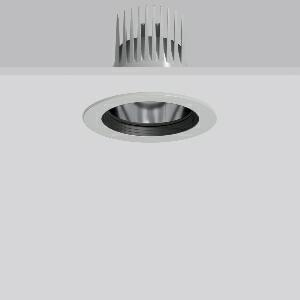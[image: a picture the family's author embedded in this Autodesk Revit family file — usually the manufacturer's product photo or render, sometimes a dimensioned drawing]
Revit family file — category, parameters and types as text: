
# Revit family: heledon_maxi_e_901759_004_94ef
name_source: partatom
category: Lighting Fixtures
units: mm (PartAtom-declared; Revit-internal decimal feet)

## family parameters
Cut with Voids When Loaded = No
Host = Face
Light Source = No
Part Type = Normal
Room Calculation Point = No
Round Connector Dimension = Use Diameter
Shared = No

## types (1)
- HELEDON maxi E (1 x LED Modul 930, 3250 lm, 3000)
    Apparent Load = 25 VA
    Approval mark = CE
    CIE Flux Codes = 97 100 100 100 100
    Color Rendering = 90
    Color Temperature = 3000
    Default Elevation = 1800 mm
    Description = Series: HELEDON maxi
Round recessed downlight. Housing: die-cast aluminium, powder-coated. Black plastic ring and recessed LED to prevent glare from the side. Optical assembly with reflector made of MIRO-Silver with 98% total light reflection for outstanding efficiency - can be changed without tools. Best colour rendering index Ra>90. Suitable for Recessed ceiling mounting. Installation without tools thanks to spring fastening system. Including separate LED converter with connecting cable 600 mm.High quality converter without flickering and stroboscopic effect. Through-wiring box (5 pole) available as accessory. The following accessories can be mounted without use of tools: interchangeable lenses, decorative glasses, honeycomb louvre, clear and frosted diffusers, white interchangeable plastic ring. 
Colour: silver
Diameter: 162 mm
Height: 3 mm
Cut-out diameter: 152 mm
Recess height: 200 mm
Luminaire: recess height: 135 mm
Lamp: LED
Socket: without socket
Colour temperature: 3000K
Colour rendering index (CRI): 92
System power: 25 W
Rated luminous flux: 3250 lm
Luminous efficiency: 130 lm/W
Control gear: Regulated power supply
Protection class: II
Type of protection: IP 20
    Height = 0 mm  [stored 0 ft]
    Lamp = 1 x LED Modul 930
    Lamp Light Flux = 3250 lm
    Lamp count = 1
    Length = 162 mm
    Lifetime = 50000 h
    Luminous efficacy = 130 lm/W
    Manufacturer = RZB
    ModVariant = No
    Model = 901759.004
    Mounting Place = Ceiling
    Mounting Type = Recessed
    Number of Poles = 1
    OnlyDefault = Yes
    Power Factor = 1
    Product Name = HELEDON maxi E
    Product group = Recessed downlights
    ProductGroupID = 402
    Protection Class = Protection class II
    Protection Degree = IP 20
    RLX_Detail_Level = 1
    RLX_Emergency_Light_Flux = 0 lm
    RLX_Emergency_Type = 0
    RLX_Emergency_Type_DB = No
    RlxData = <blob elided: 119085 chars, md5=a5e24ed4>
    Socket = socket
    Standby Power = 0 W
    System Light Flux = 3250 lm
    System Power = 25 W
    Type Comments = Product without accessories
    Type Image = 901662.004.jpg
    URL = http://relux.com
    VarID = ---
    Voltage = 230 V
    Voltage Range = 220-240 V
    Weight = 0.00 kg
    Width = 0 mm  [stored 0 ft]

note: [stored X ft] marks values corroborated as IEEE doubles in the binary element streams (Revit-internal decimal feet)

## geometry (parser evidence)
native form markers: Blend x4, Sweep x12
no freeform markers — native parametric forms only
